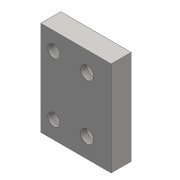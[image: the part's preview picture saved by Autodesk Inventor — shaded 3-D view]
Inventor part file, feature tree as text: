
AUTODESK INVENTOR PART (.ipt)
format: ipt  version: 2016 (Build 200138000, 138)  size: 925,696 bytes
history: native  units: mm
features: sketch x4, extrude x2, hole x2, chamfer x1, mirror x1, projected_geometry x1
ambient origin geometry x8: Origin, YZ Plane, XZ Plane, XY Plane, X Axis, Y Axis, Z Axis, Center Point
bodies: Body1 (feature_tree)
feature tree (11):
  sketch  "Sketch1"  dims[d5=4.8mm d6=4.8mm]
  extrude  "Extrusion3"  Depth=4.8mm
  chamfer  "Chamfer2"  Distance=3.0mm
  extrude  "Extrusion4"  Depth=3.0mm
  hole  "Hole1"  [1 undecoded]
  hole  "Hole3"  [1 undecoded]
  mirror  "Mirror1"
  sketch  "Sketch3"  dims[d7=3.0mm]
  sketch  "Sketch5"  dims[d8=3.0mm]
  projected_geometry  "Projected Loop1"
  sketch  "Sketch7"  dims[d9=3.0mm d10=3.0mm d11=3.0mm d12=3.0mm d17=4.25mm d19=1.5mm d20=4.3mm d21=10.0mm d22=2.0mm d23=1.5mm d24=4.3mm d25=10.0mm d26=2.0mm d35=0.5mm d37=1.5mm d48=1.0mm d49=0.2mm d50=0.2mm d51=0.2mm d52=2.0mm d53=0.0mm d54=0.2mm d55=2.0mm d56=45.0deg d60=10.0mm d63=5.0mm d64=0.0mm d65=4.0mm d66=0.0mm d67=3.2mm d68=6.0mm d69=6.0mm d70=3.5mm d71=90.0deg d72=8.0mm d73=20.594885mm d74=0.0mm d75=2.0mm d83=3.0mm d84=6.0mm d85=6.0mm d86=3.5mm d87=90.0deg d88=8.0mm d89=20.594885mm]
note: 2 required parameter values undecoded (feature->parameter linkage not recoverable at this tier; creation-order binding heuristic only, values carry confidence <= 0.55)
